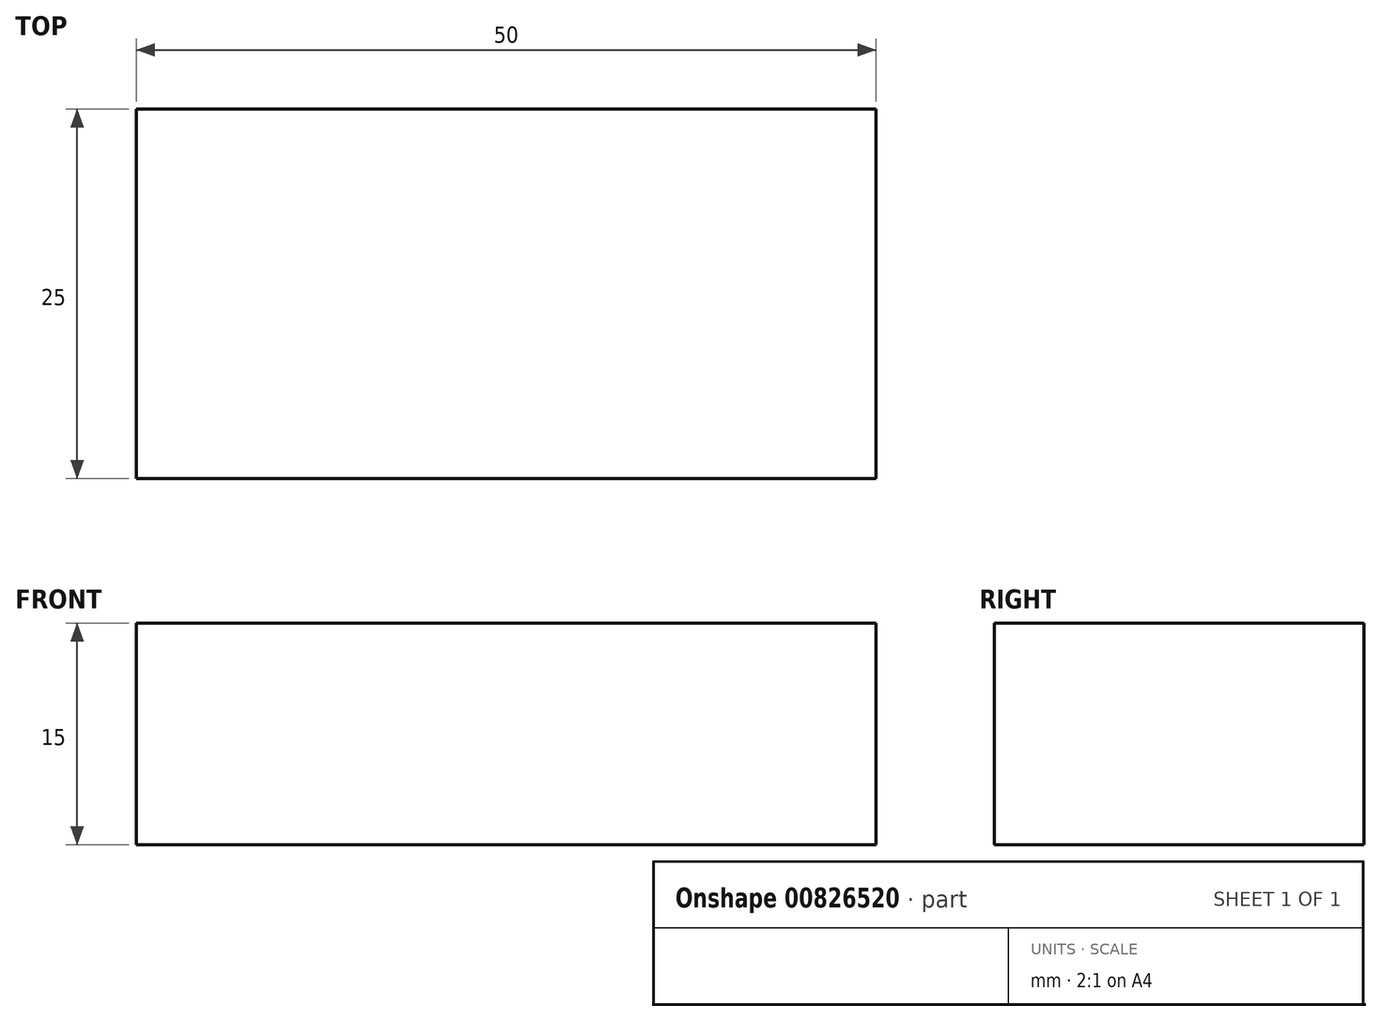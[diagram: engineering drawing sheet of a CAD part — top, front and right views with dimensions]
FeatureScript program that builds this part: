
annotation { "Feature Type Name" : "Feature", "Feature Type Description" : "" }
export const myFeature = defineFeature(function(context is Context, id is Id, definition is map)
    precondition{}
    {
        {
            var Q0;
            Q0=qCreatedBy(makeId("Front.planeOp"),FACE);
            var sketch = newSketch(context, id + "F0", { "sketchPlane" : qUnion([Q0])});
            skPoint(sketch, "E0.start.orphan", {"position": v(25, 0) * mm});
            skLineSegment(sketch, "E1", {"start": v(0, 0) * mm, "end": v(50, 0) * mm});
            skLineSegment(sketch, "E2", {"start": v(0, 0) * mm, "end": v(0, 15) * mm});
            skLineSegment(sketch, "E3", {"start": v(50, 0) * mm, "end": v(50, 15) * mm});
            skLineSegment(sketch, "E4", {"start": v(0, 15) * mm, "end": v(50, 15) * mm});
            skSolve(sketch);
        }
        {
            var Q0;
            Q0 = qSketchRegion(id + "F0", true);
            extrude(context, id + "F1", {"entities" : qUnion([Q0]), "depth" : 25 * mm, "offsetDistance" : 25 * mm});
        }
        {
            var Q0;
            Q0=makeQuery(id+"F1.opExtrude","SWEPT_FACE",FACE,{"disambiguationData":[OSD([sQuery(id+"F0.wireOp",EDGE,"E4")])]});
            var sketch = newSketch(context, id + "F2", { "sketchPlane" : qUnion([Q0])});
            skCircle(sketch, "E5", {"center": v(24.38, -12.98) * mm, "radius": 2 * mm});
            skSolve(sketch);
        }
        {
            var Q0;
            Q0=sQuery(id+"F2.wireOp",EDGE,"E5");
            extrude(context, id + "F3", {"bodyType" : ToolBodyType.SURFACE, "surfaceEntities" : qUnion([Q0]), "oppositeDirection" : true, "depth" : 14.9 * mm, "offsetDistance" : 25 * mm});
        }
    });
